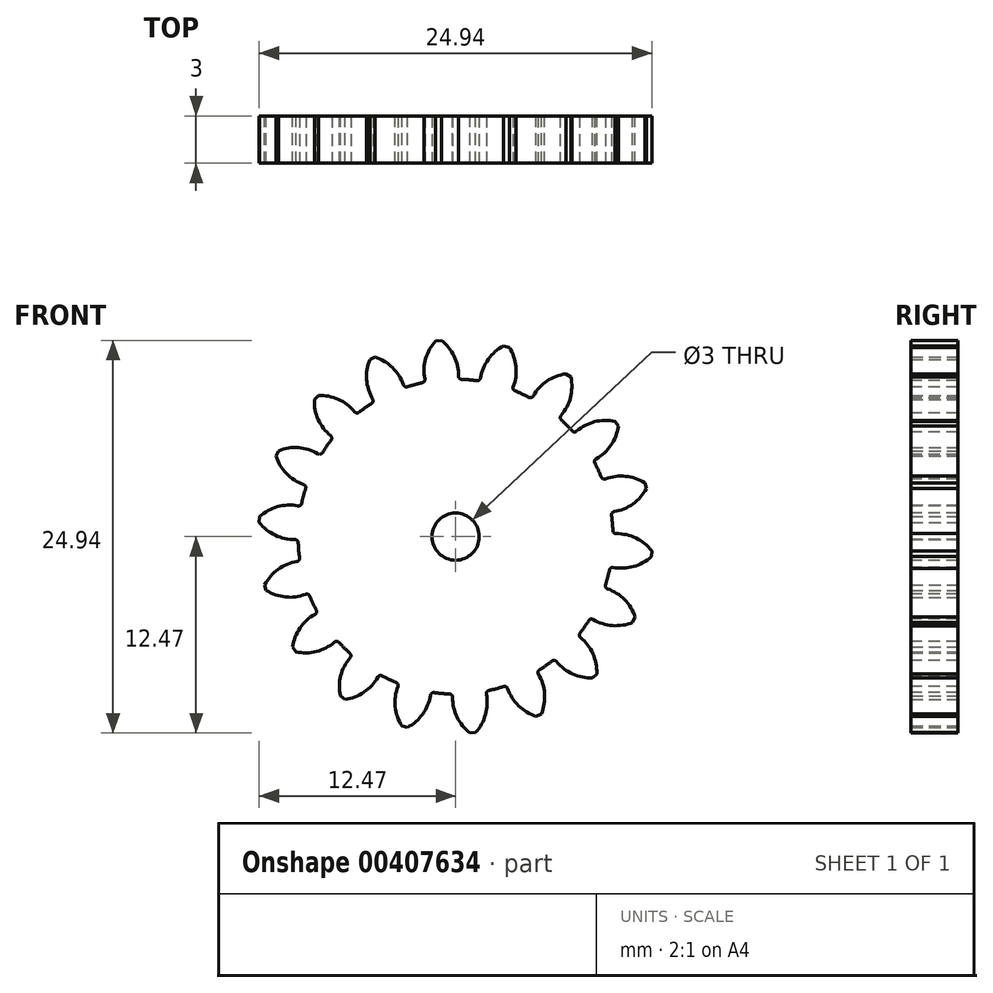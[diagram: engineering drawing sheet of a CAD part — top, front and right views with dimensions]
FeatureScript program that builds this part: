
annotation { "Feature Type Name" : "Feature", "Feature Type Description" : "" }
export const myFeature = defineFeature(function(context is Context, id is Id, definition is map)
    precondition{}
    {
        {
            var Q0;
            Q0=qCreatedBy(makeId("Front.planeOp"),FACE);
            var sketch = newSketch(context, id + "F0", { "sketchPlane" : qUnion([Q0])});
            skCircle(sketch, "E0", {"center": v(0, 0) * mm, "radius": 12.5 * mm, "construction": true});
            skCircle(sketch, "E1", {"center": v(0, 0) * mm, "radius": 11.25 * mm, "construction": true});
            skCircle(sketch, "E2", {"center": v(0, 0) * mm, "radius": 10 * mm});
            skCircle(sketch, "E3", {"center": v(0, 0) * mm, "radius": 10.57 * mm, "construction": true});
            skLineSegment(sketch, "E4", {"start": v(0, 0) * mm, "end": v(0, 26.42) * mm, "construction": true});
            skLineSegment(sketch, "E5", {"start": v(0, 0) * mm, "end": v(-2.3, 26.26) * mm, "construction": true});
            skLineSegment(sketch, "E6", {"start": v(0, 11.25) * mm, "end": v(-13.1, 11.25) * mm, "construction": true});
            skCircle(sketch, "E7", {"center": v(0, 11.25) * mm, "radius": 2.81 * mm, "construction": true});
            skCircle(sketch, "E8", {"center": v(-2.63, 10.24) * mm, "radius": 2.81 * mm, "construction": true});
            skArc(sketch, "E9", {"start": v(0.18, 10) * mm, "mid": v(-0.05, 11.37) * mm, "end": v(-0.9, 12.47) * mm});
            skArc(sketch, "E10.MirrorCS", {"start": v(-1.91, 9.82) * mm, "mid": v(-1.93, 11.2) * mm, "end": v(-1.27, 12.44) * mm});
            skLineSegment(sketch, "E11", {"start": v(-1.27, 12.44) * mm, "end": v(-0.9, 12.47) * mm});
            skSolve(sketch);
        }
        {
            var Q0;
            {var subQ0=sQuery(id+"F0.wireOp",EDGE,"E2");var subQ1=makeQuery(id+"F0.imprint","INTERSECT",VERTEX,{"derivedFrom":[subQ0,sQuery(id+"F0.wireOp",EDGE,"E9")]});Q0=makeQuery(id+"F0.imprint","IMPRINT",FACE,{"disambiguationData":[TD([[makeQuery(id+"F0.imprint","IMPRINT",EDGE,{"disambiguationData":[TD([[subQ1,-1.0]])],"derivedFrom":subQ0}),1.0]])]});}
            var Q1;
            {var subQ0=sQuery(id+"F0.wireOp",EDGE,"E9");Q1=makeQuery(id+"F0.imprint","IMPRINT",FACE,{"disambiguationData":[TD([[makeQuery(id+"F0.imprint","IMPRINT",EDGE,{"derivedFrom":subQ0}),1.0]])]});}
            extrude(context, id + "F1", {"entities" : qUnion([Q0, Q1]), "depth" : 3 * mm});
        }
        {
            var Q0;
            Q0=makeQuery(id+"F1.opExtrude","SWEPT_EDGE",EDGE,{"disambiguationData":[OSD([sQuery(id+"F0.wireOp",EDGE,"E2"),sQuery(id+"F0.wireOp",EDGE,"E9")])]});
            var Q1;
            Q1=makeQuery(id+"F1.opExtrude","SWEPT_EDGE",EDGE,{"disambiguationData":[OSD([sQuery(id+"F0.wireOp",EDGE,"E2"),sQuery(id+"F0.wireOp",EDGE,"E10.MirrorCS")])]});
            fillet(context, id + "F2", {"entities" : qUnion([Q0, Q1]), "radius" : .2 * mm, "tangentPropagation" : true, "allowEdgeOverflow" : false});
        }
        {
            var Q0;
            Q0=makeQuery(id+"F1.opExtrude","SWEPT_BODY",BODY,{"disambiguationData":[OSD([sQuery(id+"F0.wireOp",EDGE,"E2"),sQuery(id+"F0.wireOp",EDGE,"E9"),sQuery(id+"F0.wireOp",EDGE,"E10.MirrorCS"),sQuery(id+"F0.wireOp",EDGE,"E11")])]});
            var Q1;
            Q1=makeQuery(id+"F1.opExtrude","SWEPT_FACE",FACE,{"disambiguationData":[OSD([sQuery(id+"F0.wireOp",EDGE,"E2")])]});
            circularPattern(context, id + "F3", {"entities" : qUnion([Q0]), "axis" : qUnion([Q1]), "angle" : 360 * degree, "instanceCount" : 18, "equalSpace" : true});
        }
        {
            var Q0;
            Q0=makeQuery(id+"F3.opPattern","COPY",BODY,{"derivedFrom":makeQuery(id+"F1.opExtrude","SWEPT_BODY",BODY,{"disambiguationData":[OSD([sQuery(id+"F0.wireOp",EDGE,"E2"),sQuery(id+"F0.wireOp",EDGE,"E9"),sQuery(id+"F0.wireOp",EDGE,"E10.MirrorCS"),sQuery(id+"F0.wireOp",EDGE,"E11")])]}),"instanceName":"4"});
            var Q1;
            Q1=makeQuery(id+"F3.opPattern","COPY",BODY,{"derivedFrom":makeQuery(id+"F1.opExtrude","SWEPT_BODY",BODY,{"disambiguationData":[OSD([sQuery(id+"F0.wireOp",EDGE,"E2"),sQuery(id+"F0.wireOp",EDGE,"E9"),sQuery(id+"F0.wireOp",EDGE,"E10.MirrorCS"),sQuery(id+"F0.wireOp",EDGE,"E11")])]}),"instanceName":"1"});
            var Q2;
            Q2=makeQuery(id+"F3.opPattern","COPY",BODY,{"derivedFrom":makeQuery(id+"F1.opExtrude","SWEPT_BODY",BODY,{"disambiguationData":[OSD([sQuery(id+"F0.wireOp",EDGE,"E2"),sQuery(id+"F0.wireOp",EDGE,"E9"),sQuery(id+"F0.wireOp",EDGE,"E10.MirrorCS"),sQuery(id+"F0.wireOp",EDGE,"E11")])]}),"instanceName":"2"});
            var Q3;
            Q3=makeQuery(id+"F3.opPattern","COPY",BODY,{"derivedFrom":makeQuery(id+"F1.opExtrude","SWEPT_BODY",BODY,{"disambiguationData":[OSD([sQuery(id+"F0.wireOp",EDGE,"E2"),sQuery(id+"F0.wireOp",EDGE,"E9"),sQuery(id+"F0.wireOp",EDGE,"E10.MirrorCS"),sQuery(id+"F0.wireOp",EDGE,"E11")])]}),"instanceName":"5"});
            var Q4;
            Q4=makeQuery(id+"F3.opPattern","COPY",BODY,{"derivedFrom":makeQuery(id+"F1.opExtrude","SWEPT_BODY",BODY,{"disambiguationData":[OSD([sQuery(id+"F0.wireOp",EDGE,"E2"),sQuery(id+"F0.wireOp",EDGE,"E9"),sQuery(id+"F0.wireOp",EDGE,"E10.MirrorCS"),sQuery(id+"F0.wireOp",EDGE,"E11")])]}),"instanceName":"3"});
            var Q5;
            Q5=makeQuery(id+"F3.opPattern","COPY",BODY,{"derivedFrom":makeQuery(id+"F1.opExtrude","SWEPT_BODY",BODY,{"disambiguationData":[OSD([sQuery(id+"F0.wireOp",EDGE,"E2"),sQuery(id+"F0.wireOp",EDGE,"E9"),sQuery(id+"F0.wireOp",EDGE,"E10.MirrorCS"),sQuery(id+"F0.wireOp",EDGE,"E11")])]}),"instanceName":"7"});
            var Q6;
            Q6=makeQuery(id+"F3.opPattern","COPY",BODY,{"derivedFrom":makeQuery(id+"F1.opExtrude","SWEPT_BODY",BODY,{"disambiguationData":[OSD([sQuery(id+"F0.wireOp",EDGE,"E2"),sQuery(id+"F0.wireOp",EDGE,"E9"),sQuery(id+"F0.wireOp",EDGE,"E10.MirrorCS"),sQuery(id+"F0.wireOp",EDGE,"E11")])]}),"instanceName":"6"});
            var Q7;
            Q7=makeQuery(id+"F3.opPattern","COPY",BODY,{"derivedFrom":makeQuery(id+"F1.opExtrude","SWEPT_BODY",BODY,{"disambiguationData":[OSD([sQuery(id+"F0.wireOp",EDGE,"E2"),sQuery(id+"F0.wireOp",EDGE,"E9"),sQuery(id+"F0.wireOp",EDGE,"E10.MirrorCS"),sQuery(id+"F0.wireOp",EDGE,"E11")])]}),"instanceName":"8"});
            var Q8;
            Q8=makeQuery(id+"F3.opPattern","COPY",BODY,{"derivedFrom":makeQuery(id+"F1.opExtrude","SWEPT_BODY",BODY,{"disambiguationData":[OSD([sQuery(id+"F0.wireOp",EDGE,"E2"),sQuery(id+"F0.wireOp",EDGE,"E9"),sQuery(id+"F0.wireOp",EDGE,"E10.MirrorCS"),sQuery(id+"F0.wireOp",EDGE,"E11")])]}),"instanceName":"10"});
            var Q9;
            Q9=makeQuery(id+"F3.opPattern","COPY",BODY,{"derivedFrom":makeQuery(id+"F1.opExtrude","SWEPT_BODY",BODY,{"disambiguationData":[OSD([sQuery(id+"F0.wireOp",EDGE,"E2"),sQuery(id+"F0.wireOp",EDGE,"E9"),sQuery(id+"F0.wireOp",EDGE,"E10.MirrorCS"),sQuery(id+"F0.wireOp",EDGE,"E11")])]}),"instanceName":"9"});
            var Q10;
            Q10=makeQuery(id+"F3.opPattern","COPY",BODY,{"derivedFrom":makeQuery(id+"F1.opExtrude","SWEPT_BODY",BODY,{"disambiguationData":[OSD([sQuery(id+"F0.wireOp",EDGE,"E2"),sQuery(id+"F0.wireOp",EDGE,"E9"),sQuery(id+"F0.wireOp",EDGE,"E10.MirrorCS"),sQuery(id+"F0.wireOp",EDGE,"E11")])]}),"instanceName":"11"});
            var Q11;
            Q11=makeQuery(id+"F3.opPattern","COPY",BODY,{"derivedFrom":makeQuery(id+"F1.opExtrude","SWEPT_BODY",BODY,{"disambiguationData":[OSD([sQuery(id+"F0.wireOp",EDGE,"E2"),sQuery(id+"F0.wireOp",EDGE,"E9"),sQuery(id+"F0.wireOp",EDGE,"E10.MirrorCS"),sQuery(id+"F0.wireOp",EDGE,"E11")])]}),"instanceName":"12"});
            var Q12;
            Q12=makeQuery(id+"F3.opPattern","COPY",BODY,{"derivedFrom":makeQuery(id+"F1.opExtrude","SWEPT_BODY",BODY,{"disambiguationData":[OSD([sQuery(id+"F0.wireOp",EDGE,"E2"),sQuery(id+"F0.wireOp",EDGE,"E9"),sQuery(id+"F0.wireOp",EDGE,"E10.MirrorCS"),sQuery(id+"F0.wireOp",EDGE,"E11")])]}),"instanceName":"13"});
            var Q13;
            Q13=makeQuery(id+"F3.opPattern","COPY",BODY,{"derivedFrom":makeQuery(id+"F1.opExtrude","SWEPT_BODY",BODY,{"disambiguationData":[OSD([sQuery(id+"F0.wireOp",EDGE,"E2"),sQuery(id+"F0.wireOp",EDGE,"E9"),sQuery(id+"F0.wireOp",EDGE,"E10.MirrorCS"),sQuery(id+"F0.wireOp",EDGE,"E11")])]}),"instanceName":"16"});
            var Q14;
            Q14=makeQuery(id+"F3.opPattern","COPY",BODY,{"derivedFrom":makeQuery(id+"F1.opExtrude","SWEPT_BODY",BODY,{"disambiguationData":[OSD([sQuery(id+"F0.wireOp",EDGE,"E2"),sQuery(id+"F0.wireOp",EDGE,"E9"),sQuery(id+"F0.wireOp",EDGE,"E10.MirrorCS"),sQuery(id+"F0.wireOp",EDGE,"E11")])]}),"instanceName":"17"});
            var Q15;
            Q15=makeQuery(id+"F1.opExtrude","SWEPT_BODY",BODY,{"disambiguationData":[OSD([sQuery(id+"F0.wireOp",EDGE,"E2"),sQuery(id+"F0.wireOp",EDGE,"E9"),sQuery(id+"F0.wireOp",EDGE,"E10.MirrorCS"),sQuery(id+"F0.wireOp",EDGE,"E11")])]});
            var Q16;
            Q16=makeQuery(id+"F3.opPattern","COPY",BODY,{"derivedFrom":makeQuery(id+"F1.opExtrude","SWEPT_BODY",BODY,{"disambiguationData":[OSD([sQuery(id+"F0.wireOp",EDGE,"E2"),sQuery(id+"F0.wireOp",EDGE,"E9"),sQuery(id+"F0.wireOp",EDGE,"E10.MirrorCS"),sQuery(id+"F0.wireOp",EDGE,"E11")])]}),"instanceName":"15"});
            var Q17;
            Q17=makeQuery(id+"F3.opPattern","COPY",BODY,{"derivedFrom":makeQuery(id+"F1.opExtrude","SWEPT_BODY",BODY,{"disambiguationData":[OSD([sQuery(id+"F0.wireOp",EDGE,"E2"),sQuery(id+"F0.wireOp",EDGE,"E9"),sQuery(id+"F0.wireOp",EDGE,"E10.MirrorCS"),sQuery(id+"F0.wireOp",EDGE,"E11")])]}),"instanceName":"14"});
            booleanBodies(context, id + "F4", {"operationType" : BooleanOperationType.UNION, "tools" : qUnion([Q0, Q1, Q2, Q3, Q4, Q5, Q6, Q7, Q8, Q9, Q10, Q11, Q12, Q13, Q14, Q15, Q16, Q17])});
        }
        {
            var Q0;
            {var subQ0=makeQuery(id+"F1.opExtrude","CAP_FACE",FACE,{"disambiguationData":[OSD([sQuery(id+"F0.wireOp",EDGE,"E2"),sQuery(id+"F0.wireOp",EDGE,"E9"),sQuery(id+"F0.wireOp",EDGE,"E10.MirrorCS"),sQuery(id+"F0.wireOp",EDGE,"E11")])],"isStart":false});Q0=makeQuery(id+"F4.opBoolean","MERGE",FACE,{"derivedFrom":[subQ0,makeQuery(id+"F3.opPattern","COPY",FACE,{"derivedFrom":subQ0,"instanceName":"1"}),makeQuery(id+"F3.opPattern","COPY",FACE,{"derivedFrom":subQ0,"instanceName":"2"}),makeQuery(id+"F3.opPattern","COPY",FACE,{"derivedFrom":subQ0,"instanceName":"3"}),makeQuery(id+"F3.opPattern","COPY",FACE,{"derivedFrom":subQ0,"instanceName":"4"}),makeQuery(id+"F3.opPattern","COPY",FACE,{"derivedFrom":subQ0,"instanceName":"5"}),makeQuery(id+"F3.opPattern","COPY",FACE,{"derivedFrom":subQ0,"instanceName":"6"}),makeQuery(id+"F3.opPattern","COPY",FACE,{"derivedFrom":subQ0,"instanceName":"7"}),makeQuery(id+"F3.opPattern","COPY",FACE,{"derivedFrom":subQ0,"instanceName":"8"}),makeQuery(id+"F3.opPattern","COPY",FACE,{"derivedFrom":subQ0,"instanceName":"9"}),makeQuery(id+"F3.opPattern","COPY",FACE,{"derivedFrom":subQ0,"instanceName":"10"}),makeQuery(id+"F3.opPattern","COPY",FACE,{"derivedFrom":subQ0,"instanceName":"11"}),makeQuery(id+"F3.opPattern","COPY",FACE,{"derivedFrom":subQ0,"instanceName":"12"}),makeQuery(id+"F3.opPattern","COPY",FACE,{"derivedFrom":subQ0,"instanceName":"13"}),makeQuery(id+"F3.opPattern","COPY",FACE,{"derivedFrom":subQ0,"instanceName":"14"}),makeQuery(id+"F3.opPattern","COPY",FACE,{"derivedFrom":subQ0,"instanceName":"15"}),makeQuery(id+"F3.opPattern","COPY",FACE,{"derivedFrom":subQ0,"instanceName":"16"}),makeQuery(id+"F3.opPattern","COPY",FACE,{"derivedFrom":subQ0,"instanceName":"17"})]});}
            var sketch = newSketch(context, id + "F5", { "sketchPlane" : qUnion([Q0])});
            skCircle(sketch, "E12", {"center": v(0, 0) * mm, "radius": 1.5 * mm});
            skSolve(sketch);
        }
        {
            var Q0;
            Q0=makeQuery(id+"F5.imprint","IMPRINT",FACE,{"disambiguationData":[TD([[makeQuery(id+"F5.imprint","IMPRINT",EDGE,{"derivedFrom":sQuery(id+"F5.wireOp",EDGE,"E12")}),1.0]])]});
            extrude(context, id + "F6", {"entities" : qUnion([Q0]), "operationType" : NewBodyOperationType.REMOVE, "endBound" : BoundingType.THROUGH_ALL, "oppositeDirection" : true, "depth" : 25 * mm});
        }
    });
